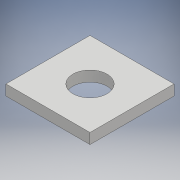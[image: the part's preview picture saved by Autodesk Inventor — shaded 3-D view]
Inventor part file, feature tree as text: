
AUTODESK INVENTOR PART (.ipt)
format: ipt  version: 2018 (Build 220112000, 112)  size: 96,256 bytes
history: native  units: mm
features: sketch x2, other x1, extrude x1, hole x1
ambient origin geometry x8: Origin, YZ Plane, XZ Plane, XY Plane, X Axis, Y Axis, Z Axis, Center Point
bodies: Body1 (feature_tree)
feature tree (5):
  other  "ソリッド1"
  extrude  "押し出し1"  Depth=32.0mm
  hole  "穴1"  [1 undecoded]
  sketch  "スケッチ1"
  sketch  "スケッチ2"
note: 1 required parameter value undecoded (feature->parameter linkage not recoverable at this tier; creation-order binding heuristic only, values carry confidence <= 0.55)
